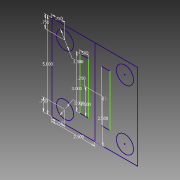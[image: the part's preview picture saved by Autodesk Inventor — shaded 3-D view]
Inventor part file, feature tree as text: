
AUTODESK INVENTOR PART (.ipt)
format: ipt  version: 2015 (Build 190159000, 159)  size: 79,360 bytes
history: native  units: in
note: dims shown in document units (in); Inventor stores cm internally (conversion verified against a paired STEP export)
features: sketch x1
ambient origin geometry x8: Origin, YZ Plane, XZ Plane, XY Plane, X Axis, Y Axis, Z Axis, Center Point
feature tree (1):
  sketch  "Sketch1"  dims[d0=5.0in d1=2.5in d2=1.0in d3=0.75in d4=0.75in d5=1.0in d6=0.75in d7=0.75in d8=3.0in d9=0.5in d10=1.5in d11=0.25in d12=2.5in]
